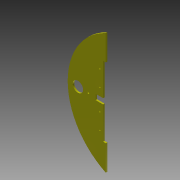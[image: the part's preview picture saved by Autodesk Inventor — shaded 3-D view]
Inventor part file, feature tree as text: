
AUTODESK INVENTOR PART (.ipt)
format: ipt  version: 2015 (Build 190159000, 159)  size: 448,000 bytes
history: native  units: mm
features: extrude x21, sketch x15, fillet x8, other x1
ambient origin geometry x8: Origin, YZ Plane, XZ Plane, XY Plane, X Axis, Y Axis, Z Axis, Center Point
bodies: Body1 (feature_tree)
feature tree (45):
  other  "Sólido1"
  sketch  "Boceto1"  dims[d0=37.0mm d1=57.0mm]
  extrude  "Extrusión1"  Depth=57.0mm
  extrude  "Extrusión2"  Depth=10.0mm
  extrude  "Extrusión3"  Depth=57.0mm
  sketch  "Boceto3"  dims[d4=20.0mm d5=57.0mm]
  extrude  "Extrusión4"  Depth=79.0mm
  extrude  "Extrusión5"  Depth=36.0mm
  extrude  "Extrusión6"  Depth=72.0mm
  extrude  "Extrusión7"  Depth=13.0mm
  fillet  "Empalme2"  Radius=3.0mm
  fillet  "Empalme3"  Radius=40.0mm
  fillet  "Empalme4"  Radius=13.0mm
  fillet  "Empalme5"  Radius=1111.0mm
  extrude  "Extrusión10"  Depth=5.0mm TaperAngle=0.0deg
  fillet  "Empalme10"  Radius=111.0mm
  sketch  "Boceto6"  dims[d6=37.0mm d7=79.0mm]
  extrude  "Extrusión11"  Depth=3.0mm
  extrude  "Extrusión12"  Depth=3.0mm
  fillet  "Empalme11"  Radius=2.0mm
  fillet  "Empalme12"  Radius=3.0mm
  extrude  "Extrusión14"  Depth=2.5mm
  extrude  "Extrusión15"  Depth=3.0mm TaperAngle=0.0deg
  extrude  "Extrusión16"  Depth=3.0mm
  extrude  "Extrusión17"  Depth=2.0mm
  extrude  "Extrusión18"  Depth=8.0mm TaperAngle=0.0deg
  extrude  "Extrusión19"  Depth=10.0mm
  extrude  "Extrusión20"  Depth=10.0mm
  extrude  "Extrusión21"  Depth=10.0mm
  extrude  "Extrusión22"  Depth=10.0mm
  extrude  "Extrusión23"  Depth=10.0mm
  fillet  "Empalme14"  Radius=20.0mm
  extrude  "Extrusión24"  Depth=10.0mm TaperAngle=0.0deg
  sketch  "Boceto2"  dims[d2=20.0mm d3=10.0mm]
  sketch  "Boceto9"  dims[d8=6.0mm d9=36.0mm]
  sketch  "Boceto10"  dims[d10=7.0mm d11=72.0mm]
  sketch  "Boceto11"  dims[d16=290.0mm d17=5.0mm d18=3.0mm d19=0.0mm d20=40.0mm d21=0.0mm d22=13.0mm d23=1111.0mm d24=0.0mm]
  sketch  "Boceto12"  dims[d25=5.0mm d26=0.0mm d27=5.0mm d28=0.0mm d29=111.0mm d30=0.0mm]
  sketch  "Boceto14"  dims[d31=3.0mm d32=0.0mm d41=1.0mm]
  sketch  "Boceto15"  dims[d42=5.0mm d43=5.0mm d44=2.0mm d47=3.0mm d48=0.0mm]
  sketch  "Boceto16"  dims[d51=1.0mm d53=2.5mm]
  sketch  "Boceto17"  dims[d54=6.5mm d55=3.0mm d56=0.0mm]
  sketch  "Boceto18"  dims[d57=3.0mm d58=0.0mm d59=1.0mm]
  sketch  "Boceto19"  dims[d60=2.0mm d67=270.0mm]
  sketch  "Boceto23"  dims[d68=10.0mm d69=0.0mm d70=292.0mm d71=300.0mm d72=270.0mm d73=10.0mm d74=6.0mm d75=3.0mm d76=0.5mm d77=35.0mm d78=3.0mm d79=0.5mm d80=6.0mm d81=35.0mm d82=40.0mm d84=360.0deg d86=8.0mm d87=0.0mm d88=20.0mm d89=75.0mm d90=40.0mm d91=140.0mm d92=20.0mm d93=20.0mm d94=2222.0mm d95=0.0mm d96=2222.0mm d97=0.0mm d98=121.760048mm d99=121.760048mm d100=5.0mm d101=70.0mm d102=70.0mm d103=10.0mm d104=0.0mm d105=15.0mm d106=5.0mm d107=5.0mm d108=10.0mm d109=0.0mm d110=3.0mm d111=10.0mm d112=0.0mm d113=0.5mm d114=10.0mm d115=0.0mm d116=15.0mm d117=8.0mm d118=10.0mm d119=0.0mm d120=4.2mm d121=111.0mm d122=0.0mm d123=4.0mm d125=21.0mm d126=10.0mm d127=0.0mm d128=20.697425mm]
